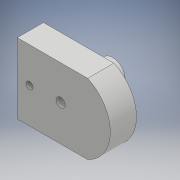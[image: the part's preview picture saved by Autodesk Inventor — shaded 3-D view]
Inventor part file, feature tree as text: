
AUTODESK INVENTOR PART (.ipt)
format: ipt  version: 2017 SP1 (Build 210196100, 196)  size: 117,248 bytes
history: native  units: mm
features: extrude x2, sketch x2, other x1, hole x1
ambient origin geometry x8: Origin, YZ Plane, XZ Plane, XY Plane, X Axis, Y Axis, Z Axis, Center Point
bodies: Body1 (feature_tree)
feature tree (6):
  other  "Bryła1"
  extrude  "Wyciągnięcie proste1"  Depth=200.0mm
  extrude  "Wyciągnięcie proste2"  Depth=200.0mm
  hole  "Otwór1"  [1 undecoded]
  sketch  "Szkic1"
  sketch  "Szkic2"
note: 1 required parameter value undecoded (feature->parameter linkage not recoverable at this tier; creation-order binding heuristic only, values carry confidence <= 0.55)
